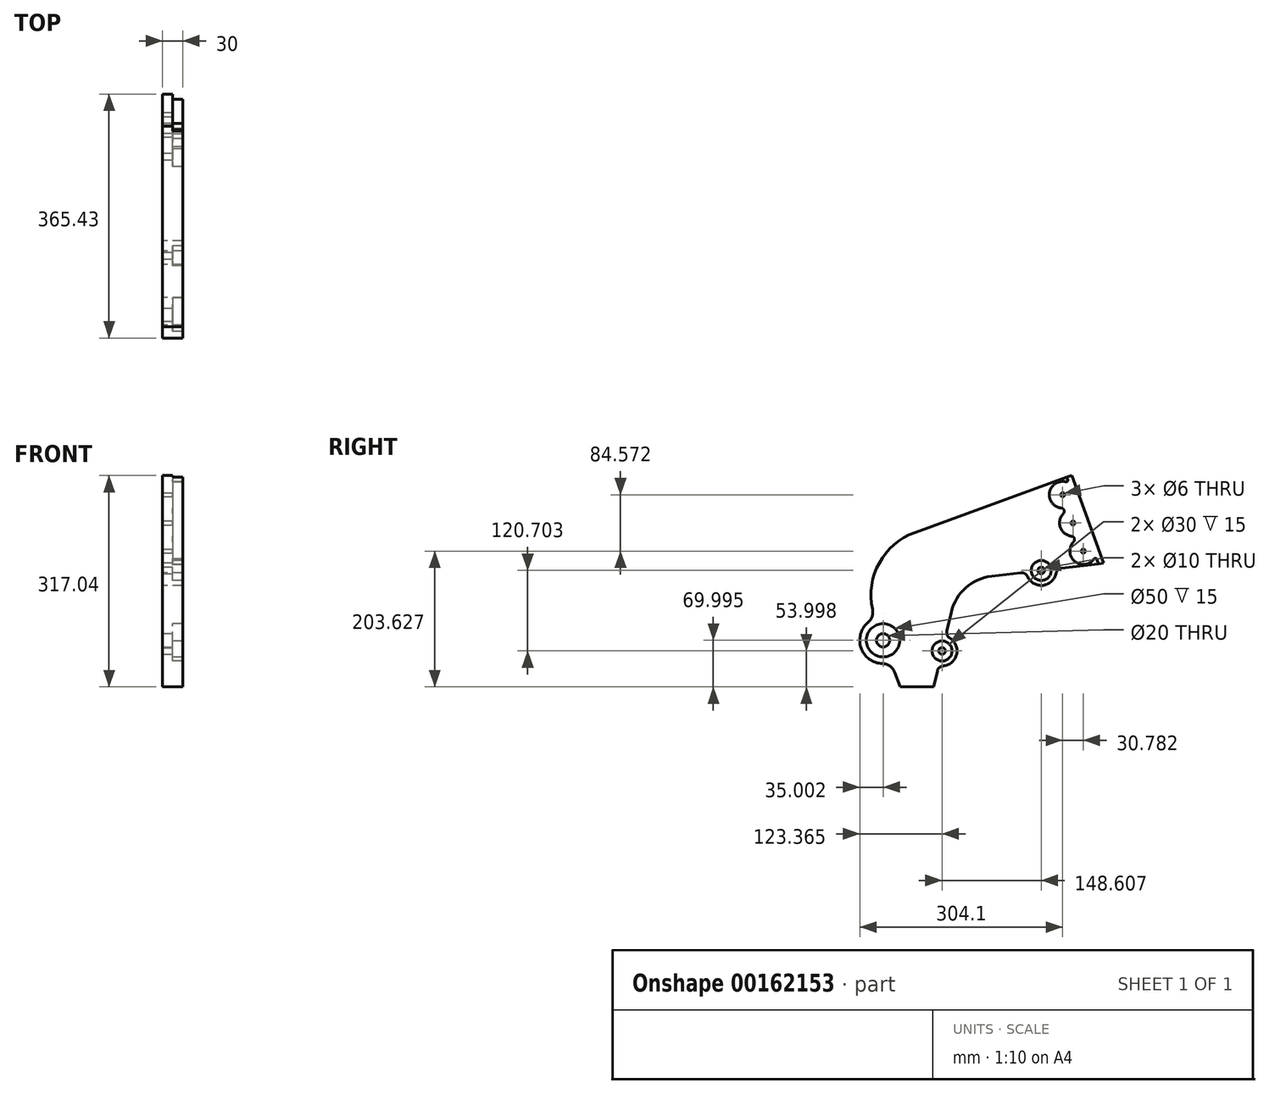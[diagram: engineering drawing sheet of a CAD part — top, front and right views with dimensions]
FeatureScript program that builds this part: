
annotation { "Feature Type Name" : "Feature", "Feature Type Description" : "" }
export const myFeature = defineFeature(function(context is Context, id is Id, definition is map)
    precondition{}
    {
        {
            var Q0;
            Q0=qCreatedBy(makeId("Right.planeOp"),FACE);
            var sketch = newSketch(context, id + "F0", { "sketchPlane" : qUnion([Q0])});
            skLineSegment(sketch, "E0", {"start": v(-120.04, -153.22) * mm, "end": v(-128, -131.37) * mm});
            skLineSegment(sketch, "E1", {"start": v(-97.9, 78.31) * mm, "end": v(137.03, 163.82) * mm});
            skLineSegment(sketch, "E2", {"start": v(137.03, 163.82) * mm, "end": v(184.91, 32.26) * mm});
            skLineSegment(sketch, "E3", {"start": v(184.91, 32.26) * mm, "end": v(122.17, 25.02) * mm});
            skLineSegment(sketch, "E4", {"start": v(-43.12, -40.4) * mm, "end": v(-49.98, -69.14) * mm});
            skLineSegment(sketch, "E5", {"start": v(-70.04, -153.22) * mm, "end": v(-120.04, -153.22) * mm});
            skPoint(sketch, "E6.visualSharp", {"position": v(-191.86, 44.11) * mm});
            skArc(sketch, "E6.filletArc", {"start": v(-97.9, 78.31) * mm, "mid": v(-151.27, 32.62) * mm, "end": v(-161.4, -36.9) * mm});
            skPoint(sketch, "E7.visualSharp", {"position": v(-31.75, 7.27) * mm});
            skArc(sketch, "E7.filletArc", {"start": v(16.95, 12.89) * mm, "mid": v(-21.49, -4.3) * mm, "end": v(-43.12, -40.4) * mm});
            skArc(sketch, "E8", {"start": v(-168.07, -56.46) * mm, "mid": v(-178.53, -94.85) * mm, "end": v(-146.33, -118.22) * mm});
            skPoint(sketch, "E9.visualSharp", {"position": v(-133.55, -116.11) * mm});
            skArc(sketch, "E9.filletArc", {"start": v(-128, -131.37) * mm, "mid": v(-135.13, -121.96) * mm, "end": v(-146.33, -118.22) * mm});
            skArc(sketch, "E10.filletArc", {"start": v(-168.07, -56.46) * mm, "mid": v(-162.02, -47.6) * mm, "end": v(-161.4, -36.9) * mm});
            skArc(sketch, "E11", {"start": v(-55.39, -121.65) * mm, "mid": v(-35.27, -104.44) * mm, "end": v(-45.45, -80) * mm});
            skArc(sketch, "E12", {"start": v(70.98, 12.15) * mm, "mid": v(94.03, -0.87) * mm, "end": v(113.51, 17.06) * mm});
            skLineSegment(sketch, "E13.trimOffspring", {"start": v(60.73, 17.94) * mm, "end": v(16.95, 12.89) * mm});
            skLineSegment(sketch, "E14.trimOffspring", {"start": v(-64.33, -129.3) * mm, "end": v(-70.04, -153.22) * mm});
            skCircle(sketch, "E15", {"center": v(91.45, 21.48) * mm, "radius": 15 * mm});
            skCircle(sketch, "E16", {"center": v(-57.16, -99.22) * mm, "radius": 15 * mm});
            skCircle(sketch, "E17", {"center": v(-57.16, -99.22) * mm, "radius": 5 * mm});
            skCircle(sketch, "E18", {"center": v(91.45, 21.48) * mm, "radius": 5 * mm});
            skPoint(sketch, "E19.visualSharp", {"position": v(113.8, 24.06) * mm});
            skArc(sketch, "E19.filletArc", {"start": v(122.17, 25.02) * mm, "mid": v(116.55, 22.45) * mm, "end": v(113.51, 17.06) * mm});
            skPoint(sketch, "E20.visualSharp", {"position": v(69.1, 18.9) * mm});
            skArc(sketch, "E20.filletArc", {"start": v(70.98, 12.15) * mm, "mid": v(66.8, 16.71) * mm, "end": v(60.73, 17.94) * mm});
            skPoint(sketch, "E21.visualSharp", {"position": v(-51.93, -77.34) * mm});
            skArc(sketch, "E21.filletArc", {"start": v(-49.98, -69.14) * mm, "mid": v(-49.48, -75.31) * mm, "end": v(-45.45, -80) * mm});
            skPoint(sketch, "E22.visualSharp", {"position": v(-62.38, -121.1) * mm});
            skArc(sketch, "E22.filletArc", {"start": v(-55.39, -121.65) * mm, "mid": v(-61.1, -124.02) * mm, "end": v(-64.33, -129.3) * mm});
            skCircle(sketch, "E23", {"center": v(-145.52, -83.22) * mm, "radius": 25 * mm});
            skCircle(sketch, "E24", {"center": v(-145.52, -83.22) * mm, "radius": 10 * mm});
            skSolve(sketch);
        }
        {
            var Q0;
            Q0=makeQuery(id+"F0.imprint","IMPRINT",FACE,{"disambiguationData":[TD([[makeQuery(id+"F0.imprint","IMPRINT",EDGE,{"derivedFrom":sQuery(id+"F0.wireOp",EDGE,"E0")}),-1.0]])]});
            extrude(context, id + "F1", {"entities" : qUnion([Q0]), "endBound" : BoundingType.SYMMETRIC, "depth" : 30 * mm});
        }
        {
            var Q0;
            Q0=makeQuery(id+"F0.imprint","IMPRINT",FACE,{"disambiguationData":[TD([[makeQuery(id+"F0.imprint","IMPRINT",EDGE,{"derivedFrom":sQuery(id+"F0.wireOp",EDGE,"E15")}),1.0]])]});
            var Q1;
            Q1=makeQuery(id+"F0.imprint","IMPRINT",FACE,{"disambiguationData":[TD([[makeQuery(id+"F0.imprint","IMPRINT",EDGE,{"derivedFrom":sQuery(id+"F0.wireOp",EDGE,"E16")}),1.0]])]});
            extrude(context, id + "F2", {"entities" : qUnion([Q0, Q1]), "operationType" : NewBodyOperationType.ADD, "oppositeDirection" : true, "depth" : 15 * mm});
        }
        {
            var Q0;
            Q0=makeQuery(id+"F0.imprint","IMPRINT",FACE,{"disambiguationData":[TD([[makeQuery(id+"F0.imprint","IMPRINT",EDGE,{"derivedFrom":sQuery(id+"F0.wireOp",EDGE,"E23")}),1.0]])]});
            extrude(context, id + "F3", {"entities" : qUnion([Q0]), "operationType" : NewBodyOperationType.ADD, "oppositeDirection" : true, "depth" : 15 * mm});
        }
        {
            var Q0;
            Q0=makeQuery(id+"F1.opExtrude","CAP_FACE",FACE,{"disambiguationData":[OSD([sQuery(id+"F0.wireOp",EDGE,"E0"),sQuery(id+"F0.wireOp",EDGE,"E1"),sQuery(id+"F0.wireOp",EDGE,"E2"),sQuery(id+"F0.wireOp",EDGE,"E3"),sQuery(id+"F0.wireOp",EDGE,"E4"),sQuery(id+"F0.wireOp",EDGE,"E5"),sQuery(id+"F0.wireOp",EDGE,"E6.filletArc"),sQuery(id+"F0.wireOp",EDGE,"E7.filletArc"),sQuery(id+"F0.wireOp",EDGE,"E8"),sQuery(id+"F0.wireOp",EDGE,"E9.filletArc"),sQuery(id+"F0.wireOp",EDGE,"E10.filletArc"),sQuery(id+"F0.wireOp",EDGE,"E11"),sQuery(id+"F0.wireOp",EDGE,"E12"),sQuery(id+"F0.wireOp",EDGE,"E13.trimOffspring"),sQuery(id+"F0.wireOp",EDGE,"E14.trimOffspring"),sQuery(id+"F0.wireOp",EDGE,"E15"),sQuery(id+"F0.wireOp",EDGE,"E16"),sQuery(id+"F0.wireOp",EDGE,"E19.filletArc"),sQuery(id+"F0.wireOp",EDGE,"E20.filletArc"),sQuery(id+"F0.wireOp",EDGE,"E21.filletArc"),sQuery(id+"F0.wireOp",EDGE,"E22.filletArc"),sQuery(id+"F0.wireOp",EDGE,"E23")])],"isStart":false});
            var sketch = newSketch(context, id + "F4", { "sketchPlane" : qUnion([Q0])});
            skLineSegment(sketch, "E25", {"start": v(129.98, 161.25) * mm, "end": v(131.28, 157.69) * mm});
            skArc(sketch, "E26", {"start": v(128.33, 154.4) * mm, "mid": v(103.87, 138.38) * mm, "end": v(121.54, 115.08) * mm});
            skArc(sketch, "E27", {"start": v(124.62, 106.63) * mm, "mid": v(120.18, 85.85) * mm, "end": v(136.94, 72.8) * mm});
            skArc(sketch, "E28", {"start": v(140.01, 64.34) * mm, "mid": v(141.45, 35.13) * mm, "end": v(170.5, 38.58) * mm});
            skLineSegment(sketch, "E29.trimOffspring", {"start": v(174.86, 37.96) * mm, "end": v(177.25, 31.38) * mm});
            skArc(sketch, "E30.filletArc", {"start": v(124.62, 106.63) * mm, "mid": v(125.73, 111.82) * mm, "end": v(121.54, 115.08) * mm});
            skArc(sketch, "E31.filletArc", {"start": v(140.01, 64.34) * mm, "mid": v(141.12, 69.53) * mm, "end": v(136.94, 72.8) * mm});
            skPoint(sketch, "E32.visualSharp", {"position": v(133.15, 152.54) * mm});
            skArc(sketch, "E32.filletArc", {"start": v(128.33, 154.4) * mm, "mid": v(130.79, 155.17) * mm, "end": v(131.28, 157.69) * mm});
            skPoint(sketch, "E33.visualSharp", {"position": v(172.98, 43.1) * mm});
            skArc(sketch, "E33.filletArc", {"start": v(174.86, 37.96) * mm, "mid": v(172.86, 39.58) * mm, "end": v(170.5, 38.58) * mm});
            skLineSegment(sketch, "E34", {"start": v(129.98, 161.25) * mm, "end": v(137.03, 163.82) * mm});
            skLineSegment(sketch, "E35", {"start": v(137.03, 163.82) * mm, "end": v(184.91, 32.26) * mm});
            skLineSegment(sketch, "E36", {"start": v(184.91, 32.26) * mm, "end": v(177.25, 31.38) * mm});
            skSolve(sketch);
        }
        {
            var Q0;
            Q0=sQuery(id+"F4.wireOp",VERTEX,"E26.center");
            var Q1;
            Q1=sQuery(id+"F4.wireOp",VERTEX,"E27.center");
            var Q2;
            Q2=sQuery(id+"F4.wireOp",VERTEX,"E28.center");
            var Q3;
            Q3=makeQuery(id+"F1.opExtrude","SWEPT_BODY",BODY,{"disambiguationData":[OSD([sQuery(id+"F0.wireOp",EDGE,"E0"),sQuery(id+"F0.wireOp",EDGE,"E1"),sQuery(id+"F0.wireOp",EDGE,"E2"),sQuery(id+"F0.wireOp",EDGE,"E3"),sQuery(id+"F0.wireOp",EDGE,"E4"),sQuery(id+"F0.wireOp",EDGE,"E5"),sQuery(id+"F0.wireOp",EDGE,"E6.filletArc"),sQuery(id+"F0.wireOp",EDGE,"E7.filletArc"),sQuery(id+"F0.wireOp",EDGE,"E8"),sQuery(id+"F0.wireOp",EDGE,"E9.filletArc"),sQuery(id+"F0.wireOp",EDGE,"E10.filletArc"),sQuery(id+"F0.wireOp",EDGE,"E11"),sQuery(id+"F0.wireOp",EDGE,"E12"),sQuery(id+"F0.wireOp",EDGE,"E13.trimOffspring"),sQuery(id+"F0.wireOp",EDGE,"E14.trimOffspring"),sQuery(id+"F0.wireOp",EDGE,"E15"),sQuery(id+"F0.wireOp",EDGE,"E16"),sQuery(id+"F0.wireOp",EDGE,"E19.filletArc"),sQuery(id+"F0.wireOp",EDGE,"E20.filletArc"),sQuery(id+"F0.wireOp",EDGE,"E21.filletArc"),sQuery(id+"F0.wireOp",EDGE,"E22.filletArc"),sQuery(id+"F0.wireOp",EDGE,"E23")])]});
            hole(context, id + "F5", {"style" : HoleStyle.SIMPLE, "endStyle" : HoleEndStyle.THROUGH, "holeDiameter" : 6 * mm, "locations" : qUnion([Q0, Q1, Q2]), "scope" : qUnion([Q3]), "isTappedThrough" : true});
        }
        {
            var Q0;
            Q0=makeQuery(id+"F4.imprint","IMPRINT",FACE,{"disambiguationData":[TD([[makeQuery(id+"F4.imprint","IMPRINT",EDGE,{"derivedFrom":sQuery(id+"F4.wireOp",EDGE,"E25")}),1.0]])]});
            extrude(context, id + "F6", {"entities" : qUnion([Q0]), "operationType" : NewBodyOperationType.REMOVE, "oppositeDirection" : true, "depth" : 15 * mm});
        }
    });
